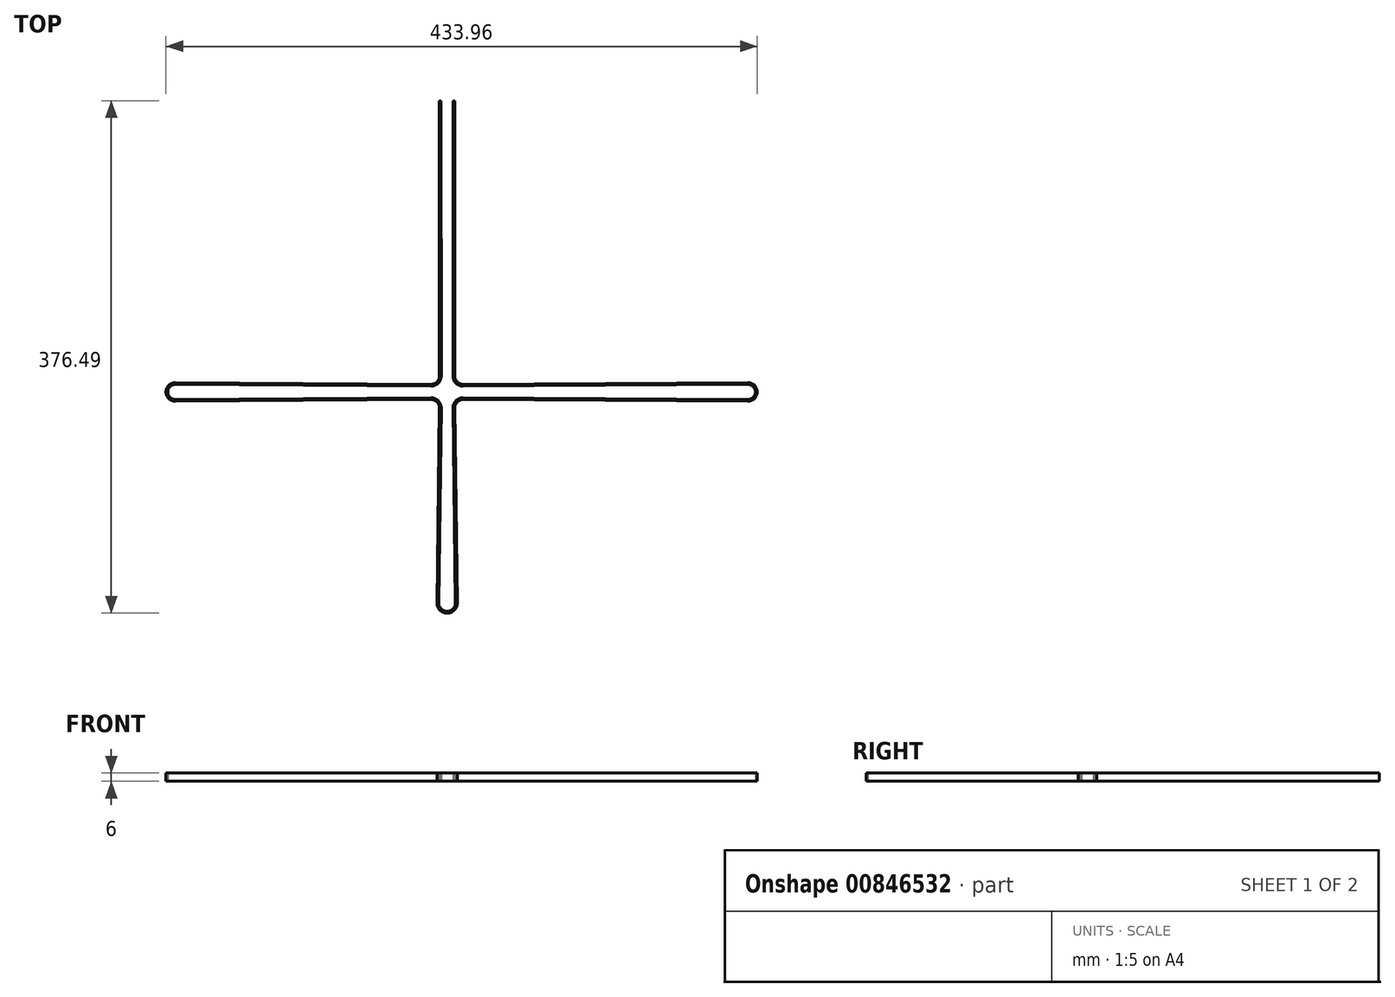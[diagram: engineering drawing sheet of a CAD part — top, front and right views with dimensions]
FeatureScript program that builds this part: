
annotation { "Feature Type Name" : "Feature", "Feature Type Description" : "" }
export const myFeature = defineFeature(function(context is Context, id is Id, definition is map)
    precondition{}
    {
        {
            var Q0;
            Q0=qCreatedBy(makeId("Top.planeOp"),FACE);
            var sketch = newSketch(context, id + "F0", { "sketchPlane" : qUnion([Q0])});
            skLineSegment(sketch, "E0.bottom", {"start": v(11.75, 11.75) * mm, "end": v(-11.75, 11.75) * mm, "construction": true});
            skLineSegment(sketch, "E0.top", {"start": v(11.75, -11.75) * mm, "end": v(-11.75, -11.75) * mm, "construction": true});
            skLineSegment(sketch, "E0.left", {"start": v(11.75, 11.75) * mm, "end": v(11.75, -11.75) * mm, "construction": true});
            skLineSegment(sketch, "E0.right", {"start": v(-11.75, 11.75) * mm, "end": v(-11.75, -11.75) * mm, "construction": true});
            skPoint(sketch, "E0.middle", {"position": v(0, 0) * mm});
            skArc(sketch, "E1", {"start": v(-11.79, 5.64) * mm, "mid": v(-7.44, 7.42) * mm, "end": v(-5.64, 11.75) * mm});
            skArc(sketch, "E2", {"start": v(-5.64, -11.83) * mm, "mid": v(-7.42, -7.44) * mm, "end": v(-11.79, -5.64) * mm});
            skLineSegment(sketch, "E3", {"start": v(0, 0) * mm, "end": v(-199.5, 0) * mm, "construction": true});
            skLineSegment(sketch, "E4", {"start": v(0, 0) * mm, "end": v(0, 214) * mm, "construction": true});
            skLineSegment(sketch, "E5", {"start": v(0, 0) * mm, "end": v(0, -155) * mm, "construction": true});
            skLineSegment(sketch, "E6", {"start": v(0, 0) * mm, "end": v(220.7, 0) * mm, "construction": true});
            skCircle(sketch, "E7", {"center": v(-199.5, 0) * mm, "radius": 6.11 * mm, "construction": true});
            skArc(sketch, "E8", {"start": v(-6.1, -154.92) * mm, "mid": v(0, -161.11) * mm, "end": v(6.1, -154.92) * mm});
            skLineSegment(sketch, "E9", {"start": v(-5.75, 214) * mm, "end": v(5.75, 214) * mm, "construction": true});
            skPoint(sketch, "E10", {"position": v(0, 214) * mm});
            skArc(sketch, "E11", {"start": v(-199.46, -5.48) * mm, "mid": v(-204.98, 0) * mm, "end": v(-199.46, 5.48) * mm});
            skArc(sketch, "E12", {"start": v(-199.46, 6.86) * mm, "mid": v(-206.36, 0) * mm, "end": v(-199.46, -6.86) * mm});
            skLineSegment(sketch, "E13", {"start": v(-194.02, 0) * mm, "end": v(-199.5, 0) * mm, "construction": true});
            skPoint(sketch, "E14", {"position": v(-193.4, 0) * mm});
            skPoint(sketch, "E15", {"position": v(-192.64, 0) * mm});
            skLineSegment(sketch, "E16", {"start": v(-5.64, 11.75) * mm, "end": v(-5.75, 214) * mm});
            skPoint(sketch, "E17", {"position": v(-4.37, 214) * mm});
            skPoint(sketch, "E18.MirrorP", {"position": v(4.37, 214) * mm});
            skLineSegment(sketch, "E19", {"start": v(-4.37, 214) * mm, "end": v(-4.26, 11.75) * mm});
            skLineSegment(sketch, "E20", {"start": v(-5.75, 214) * mm, "end": v(-4.37, 214) * mm});
            skArc(sketch, "E21", {"start": v(-11.8, 4.26) * mm, "mid": v(-6.47, 6.44) * mm, "end": v(-4.26, 11.75) * mm});
            skArc(sketch, "E22", {"start": v(-4.26, -11.85) * mm, "mid": v(-6.44, -6.47) * mm, "end": v(-11.8, -4.26) * mm});
            skLineSegment(sketch, "E23", {"start": v(-5.64, -11.83) * mm, "end": v(-7.49, -154.9) * mm});
            skArc(sketch, "E24", {"start": v(-7.49, -154.9) * mm, "mid": v(0, -162.5) * mm, "end": v(7.49, -154.9) * mm});
            skLineSegment(sketch, "E25", {"start": v(-4.26, -11.85) * mm, "end": v(-6.1, -154.92) * mm});
            skLineSegment(sketch, "E26", {"start": v(-11.79, 5.64) * mm, "end": v(-199.46, 6.86) * mm});
            skLineSegment(sketch, "E27", {"start": v(-11.8, 4.26) * mm, "end": v(-199.46, 5.48) * mm});
            skLineSegment(sketch, "E28", {"start": v(-11.8, -4.26) * mm, "end": v(-199.46, -5.48) * mm});
            skLineSegment(sketch, "E29", {"start": v(-11.79, -5.64) * mm, "end": v(-199.46, -6.86) * mm});
            skLineSegment(sketch, "E30.MirrorCS", {"start": v(5.75, 214) * mm, "end": v(4.37, 214) * mm});
            skLineSegment(sketch, "E31.MirrorCS", {"start": v(4.37, 214) * mm, "end": v(4.26, 11.75) * mm});
            skLineSegment(sketch, "E32.MirrorCS", {"start": v(5.64, 11.75) * mm, "end": v(5.75, 214) * mm});
            skArc(sketch, "E33.MirrorCS", {"start": v(11.79, 5.64) * mm, "mid": v(7.44, 7.42) * mm, "end": v(5.64, 11.75) * mm});
            skArc(sketch, "E34.MirrorCS", {"start": v(11.8, 4.26) * mm, "mid": v(6.47, 6.44) * mm, "end": v(4.26, 11.75) * mm});
            skArc(sketch, "E35.MirrorCS", {"start": v(4.26, -11.85) * mm, "mid": v(6.44, -6.47) * mm, "end": v(11.8, -4.26) * mm});
            skArc(sketch, "E36.MirrorCS", {"start": v(5.64, -11.83) * mm, "mid": v(7.42, -7.44) * mm, "end": v(11.79, -5.64) * mm});
            skLineSegment(sketch, "E37.MirrorCS", {"start": v(4.26, -11.85) * mm, "end": v(6.1, -154.92) * mm});
            skLineSegment(sketch, "E38.MirrorCS", {"start": v(5.64, -11.83) * mm, "end": v(7.49, -154.9) * mm});
            skLineSegment(sketch, "E39", {"start": v(-199.5, 0) * mm, "end": v(-199.46, -12.87) * mm, "construction": true});
            skLineSegment(sketch, "E40", {"start": v(-199.46, -12.87) * mm, "end": v(220.7, -12.87) * mm, "construction": true});
            skLineSegment(sketch, "E41", {"start": v(220.7, -12.87) * mm, "end": v(220.7, 0) * mm, "construction": true});
            skLineSegment(sketch, "E42", {"start": v(10.62, 55.58) * mm, "end": v(10.62, -12.87) * mm, "construction": true});
            skArc(sketch, "E43.MirrorCS", {"start": v(220.7, -5.48) * mm, "mid": v(226.22, 0) * mm, "end": v(220.7, 5.48) * mm});
            skArc(sketch, "E44.MirrorCS", {"start": v(220.7, 6.86) * mm, "mid": v(227.6, 0) * mm, "end": v(220.7, -6.86) * mm});
            skLineSegment(sketch, "E45", {"start": v(11.79, 5.64) * mm, "end": v(220.7, 6.86) * mm});
            skLineSegment(sketch, "E46", {"start": v(11.8, 4.26) * mm, "end": v(220.7, 5.48) * mm});
            skLineSegment(sketch, "E47", {"start": v(11.8, -4.26) * mm, "end": v(220.7, -5.48) * mm});
            skLineSegment(sketch, "E48", {"start": v(11.79, -5.64) * mm, "end": v(220.7, -6.86) * mm});
            skSolve(sketch);
        }
        {
            var Q0;
            Q0=qSketchRegion(id+"F0",true);
            extrude(context, id + "F1", {"entities" : qUnion([Q0]), "depth" : 6 * mm, "offsetDistance" : 25 * mm});
        }
    });
